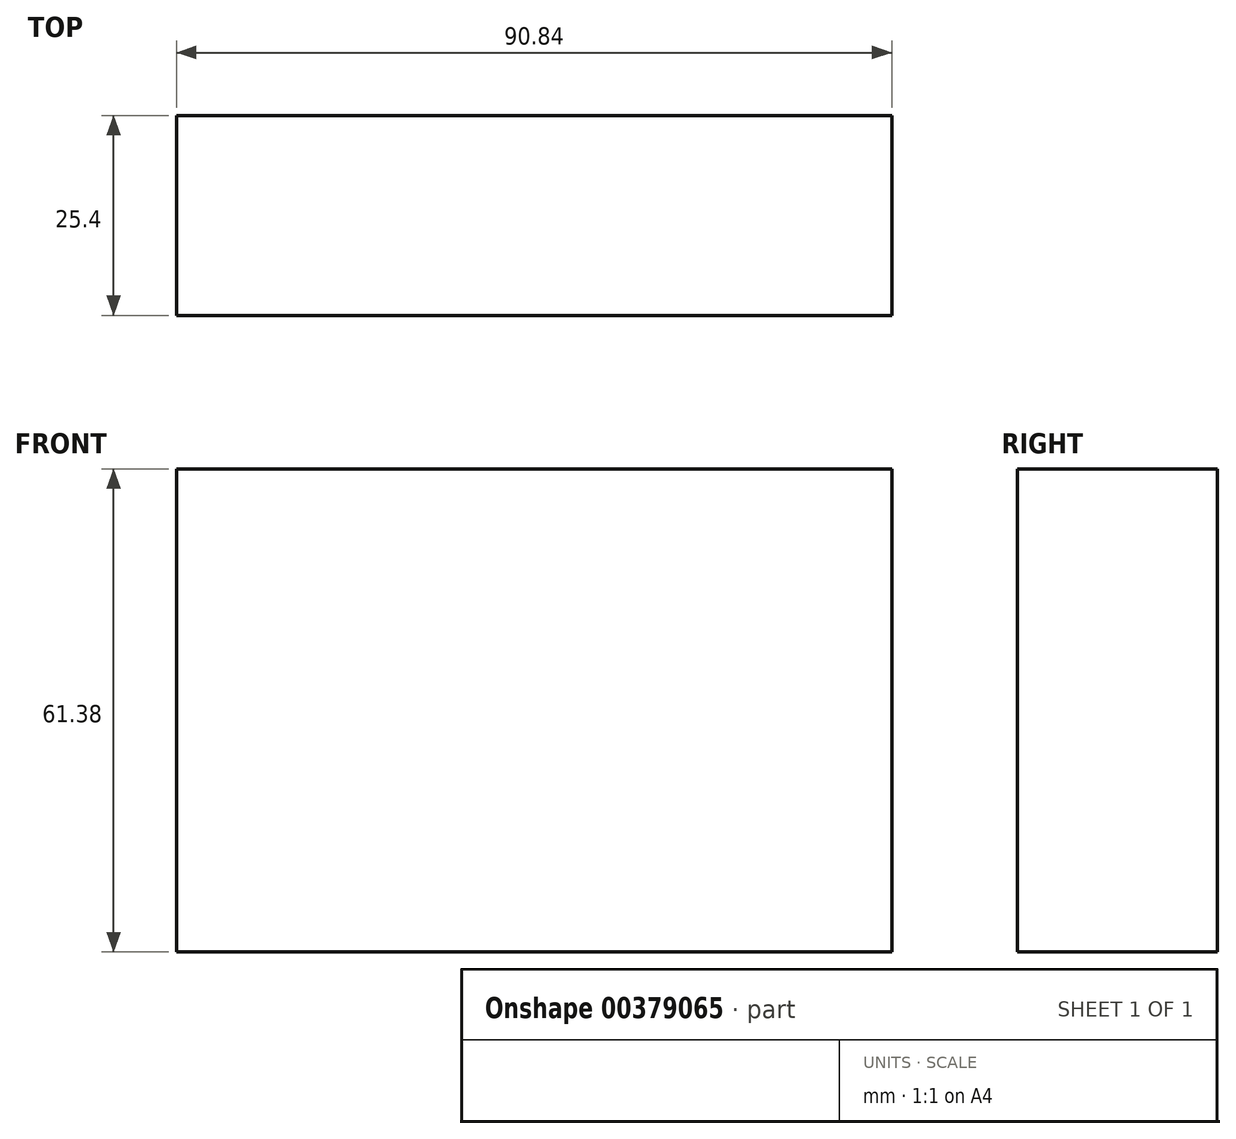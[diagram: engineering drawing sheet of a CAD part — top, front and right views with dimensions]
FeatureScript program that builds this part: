
annotation { "Feature Type Name" : "Feature", "Feature Type Description" : "" }
export const myFeature = defineFeature(function(context is Context, id is Id, definition is map)
    precondition{}
    {
        {
            var Q0;
            Q0=qCreatedBy(makeId("Front.planeOp"),FACE);
            var sketch = newSketch(context, id + "F0", { "sketchPlane" : qUnion([Q0])});
            skLineSegment(sketch, "E0.bottom", {"start": v(-125.12, 99.12) * mm, "end": v(-34.28, 99.12) * mm});
            skLineSegment(sketch, "E0.top", {"start": v(-125.12, 37.74) * mm, "end": v(-34.28, 37.74) * mm});
            skLineSegment(sketch, "E0.left", {"start": v(-125.12, 99.12) * mm, "end": v(-125.12, 37.74) * mm});
            skLineSegment(sketch, "E0.right", {"start": v(-34.28, 99.12) * mm, "end": v(-34.28, 37.74) * mm});
            skSolve(sketch);
        }
        {
            var Q0;
            Q0 = qSketchRegion(id + "F0", true);
            extrude(context, id + "F1", {"entities" : qUnion([Q0]), "depth" : 25.4 * mm});
        }
    });
